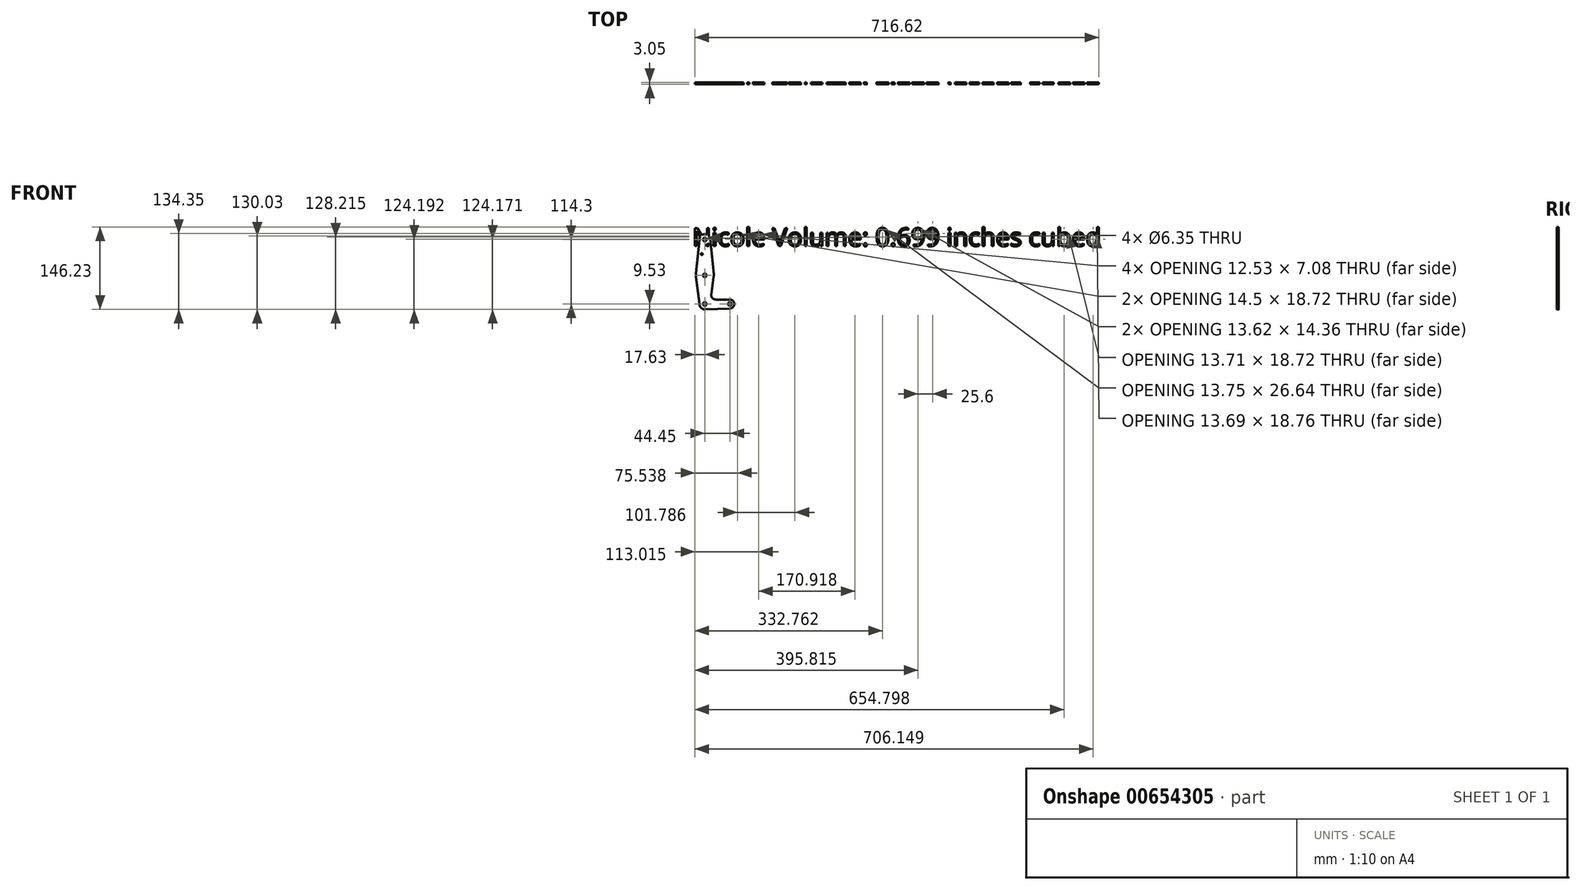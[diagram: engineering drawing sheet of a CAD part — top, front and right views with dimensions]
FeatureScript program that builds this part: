
annotation { "Feature Type Name" : "Feature", "Feature Type Description" : "" }
export const myFeature = defineFeature(function(context is Context, id is Id, definition is map)
    precondition{}
    {
        {
            var Q0;
            Q0=qCreatedBy(makeId("Front.planeOp"),FACE);
            var sketch = newSketch(context, id + "F0", { "sketchPlane" : qUnion([Q0])});
            skLineSegment(sketch, "E0", {"start": v(0, 50.8) * mm, "end": v(0, 0) * mm});
            skLineSegment(sketch, "E1", {"start": v(0, 0) * mm, "end": v(0, 114.3) * mm, "construction": true});
            skLineSegment(sketch, "E2", {"start": v(44.45, 0) * mm, "end": v(0, 0) * mm, "construction": true});
            skCircle(sketch, "E3", {"center": v(0, 114.3) * mm, "radius": 9.53 * mm});
            skCircle(sketch, "E4", {"center": v(0, 50.8) * mm, "radius": 15.88 * mm});
            skCircle(sketch, "E5", {"center": v(44.45, 0) * mm, "radius": 7.94 * mm});
            skCircle(sketch, "E6", {"center": v(0, 0) * mm, "radius": 9.53 * mm});
            skLineSegment(sketch, "E7", {"start": v(15.82, 52.15) * mm, "end": v(9.47, 115.31) * mm});
            skLineSegment(sketch, "E8", {"start": v(-15.86, 50.03) * mm, "end": v(-9.52, 114.3) * mm});
            skLineSegment(sketch, "E9", {"start": v(15.82, 52.15) * mm, "end": v(15.82, 49.45) * mm});
            skLineSegment(sketch, "E10", {"start": v(0, 0) * mm, "end": v(9.08, 0) * mm});
            skLineSegment(sketch, "E11", {"start": v(44.7, 7.93) * mm, "end": v(19.27, 7.93) * mm});
            skPoint(sketch, "E12.orphan", {"position": v(-9.53, 0) * mm});
            skLineSegment(sketch, "E13", {"start": v(11.4, 16.96) * mm, "end": v(15.82, 49.45) * mm});
            skLineSegment(sketch, "E14", {"start": v(-9.53, 0) * mm, "end": v(-15.86, 50.03) * mm});
            skPoint(sketch, "E15.end.orphan", {"position": v(0, -7.9) * mm});
            skLineSegment(sketch, "E16", {"start": v(45.14, -7.9) * mm, "end": v(0, -9.52) * mm});
            skLineSegment(sketch, "E17.trimOffspring", {"start": v(43.76, -7.9) * mm, "end": v(45.14, -7.9) * mm});
            skCircle(sketch, "E18", {"center": v(0, 114.3) * mm, "radius": 3.18 * mm});
            skCircle(sketch, "E19", {"center": v(0, 50.8) * mm, "radius": 3.17 * mm});
            skCircle(sketch, "E20", {"center": v(0, 0) * mm, "radius": 3.18 * mm});
            skCircle(sketch, "E21", {"center": v(44.45, 0) * mm, "radius": 3.18 * mm});
            skCircle(sketch, "E22", {"center": v(-5.4, 88.47) * mm, "radius": 1.59 * mm});
            skArc(sketch, "E23.filletArc", {"start": v(11.4, 16.96) * mm, "mid": v(13.28, 10.66) * mm, "end": v(19.27, 7.93) * mm});
            skText(sketch, "E24", { "text": "Nicole Volume: 0.699 inches cubed ", "fontName": "OpenSans-Regular.ttf"});
            const initialGuessF0  = {"E24": [-0.02202, 0.10268, 1, 0, 0.03224]};
            skSetInitialGuess(sketch, initialGuessF0);
            skSolve(sketch);
        }
        {
            var Q0;
            Q0 = qSketchRegion(id + "F0", true);
            extrude(context, id + "F1", {"entities" : qUnion([Q0]), "depth" : 3.05 * mm, "offsetDistance" : 25.4 * mm});
        }
    });
